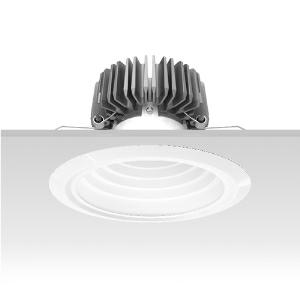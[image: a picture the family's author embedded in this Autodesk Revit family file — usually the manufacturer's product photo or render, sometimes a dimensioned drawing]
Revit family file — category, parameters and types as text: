
# Revit family: 3f_filippi_-_3f_reno_bianco_ampio_3f_filippi_-_30641_a01025_-_3f_reno_200_wh_4000-930_wide___vt_wh_974e
name_source: partatom
category: Lighting Fixtures
units: mm (PartAtom-declared; Revit-internal decimal feet)

## family parameters
Cut with Voids When Loaded = No
Host = Face
Light Source = No
Part Type = Normal
Room Calculation Point = No
Round Connector Dimension = Use Diameter
Shared = No

## types (1)
- 3F Filippi - 3F Reno Bianco Ampio (1 x LED, 3064 lm, 43 W, 3000 K)
    Apparent Load = 43 VA
    Approval mark = CE
    CIE Flux Codes = 75 94 99 100 100
    Color Rendering = 90
    Color Temperature = 3000 K
    Control Gear = Electronic ballast
    Default Elevation = 1800 mm
    Description = ILLUMINOTECHNICAL
Luminous efficiency 100% (DLOR 100%, ULOR 0%).
Initial luminous flux of the luminaire 3064 lm.
Direct symmetric wide distribution.
Installation Interdistance Transv.D = 1.56 x hu - Long.D = 1.56 x hu.
Tabular UGR (CIE 117 - 4H-8H; S=0.25H; 70/50/20): RUG 22.4 - 22.3.
Beam angle: 74° - 74°.
Luminous efficacy 71 lm/W.
Lifetime (L90/B10): 30000 h. (tq+25°C)
Lifetime (L85/B10): 50000 h. (tq+25°C)
Lifetime (L70/B10): 80000 h. (tq+25°C)
Sudden decreased luminous flux after 50000 hours: 0% (C0).
Photobiological safety in compliance with IEC/TR 62778: RG1 low risk, (IEC 62471).
In compliance with IEC/EN 62722-2-1 - IEC/EN 62717 standards.

SOURCE
Compact LED module 4000/930.
Energy efficiency class (UE 2019/2020 - UE 2019/2015): F.
CIE 13.3 Colour rendering index: CRI >90 (R9 >50%).
IES TM-30 Fidelity Index: Rf = 92 Rg = 101.
CCT nominal colour temperature 3000 K.
Colour initial tolerance (MacAdam): SDCM 3.
Zhaga Book 3 compliant.

MECHANICAL
Passive heat dissipator in die-casting aluminium, oversized, for optimum thermal management of the LED module.
Parabolic element with graduated/concentric rings in white polycarbonate.
Transparent external lens with glossy and satin differentiated surfaces, with a cooling and anti-insect system in methacrylate (PMMA).
Fastening spring clips in stainless steel.
Dimensions: diameter 226 mm, height 146 mm. Weight 1.705 kg.
IP44 protection degree for exposed part, IP20 for recessed part.
Mechanical strength to impacts IK06 (1 joule).
Glow-wire test resistance 650°C.

ELECTRICAL
Wiring on a separate unit.
Halogen Free electronic wiring 230V-50/60Hz, power factor 0.95, THD <25%, constant output current, SELV, class II, 1 driver.
Power of the luminaire 43 W.
ENEC - CE.
SAFE FLICKER: PstLM=<1 and SVM=<0.4 (IEC TR 61547-1 and IEC TR 63158), to ensure a more comfortable and safe light.
Luminaire compliant with EN 60598-2-22 for power supply from a centralised emergency system CPSS (Central Power Supply System), not incorporated in the luminaire - high risk areas excluded. The default power and flux are 100% in AC and 100% in DC.
Ambient temperature from 0°C to +25°C.
Temperature class T6 max 85°C.
Relative humidity UR: <85%.

INSTALLATION
Pull-up recessed fitting.
False ceiling carving: 200 mm.
All accessories dedicated to this product are available on the Catalog and on our website www.3F-Filippi.com.

ACCESSORIES
A01025 - VT transparent glass, tempered, not flammable, locked and in line with the trim, in white polycarbonate.

APPLICATIONS
Environments: architectural, commercial, exhibition areas, transit areas, corridors, shops, display windows, service areas.
In false ceilings with narrow voids.

WARNING
Luminaire designed for disposal/recycling at end-of-life.
Replaceable (LED only) light source by a professional. Replaceable control gear by a professional.
    Height = 0 mm  [stored 0 ft]
    Lamp = 1 x LED
    Lamp Light Flux = 3064 lm
    Lamp Power = 43 W
    Lamp count = 1
    Length = 226 mm
    Lifetime = 50000 h
    Luminous efficacy = 71 lm/W
    Manufacturer = 3F Filippi
    ModVariant = No
    Model = 3F Filippi - 30641+A01025 - 3F Reno 200 WH 4000-930 WIDE + VT WH
    Mounting Place = Ceiling
    Mounting Type = Recessed
    Number of Poles = 1
    OnlyDefault = Yes
    Power Factor = 1
    Product Name = 3F Filippi - 3F Reno Bianco Ampio
    Product group = recessed luminaire
    ProductGroupID = 4
    Protection Class = Protection class II
    Protection Degree = IP 20
    RLX_Detail_Level = 1
    RLX_Emergency_Light_Flux = 0 lm
    RLX_Emergency_Type = 0
    RLX_Emergency_Type_DB = No
    RlxData = <blob elided: 95665 chars, md5=a6347173>
    Socket = socket
    Standby Power = 0 W
    System Light Flux = 3064 lm
    System Power = 43 W
    Type Comments = Product without accessories
    Type Image = 3ffilippi_3f_reno_200_wh__a01025.jpg
    URL = http://relux.com
    VarID = ---
    Voltage = 0 V
    Weight = 0.00 kg
    Width = 0 mm  [stored 0 ft]

note: [stored X ft] marks values corroborated as IEEE doubles in the binary element streams (Revit-internal decimal feet)

## geometry (parser evidence)
native form markers: Blend x4, Sweep x10
no freeform markers — native parametric forms only
